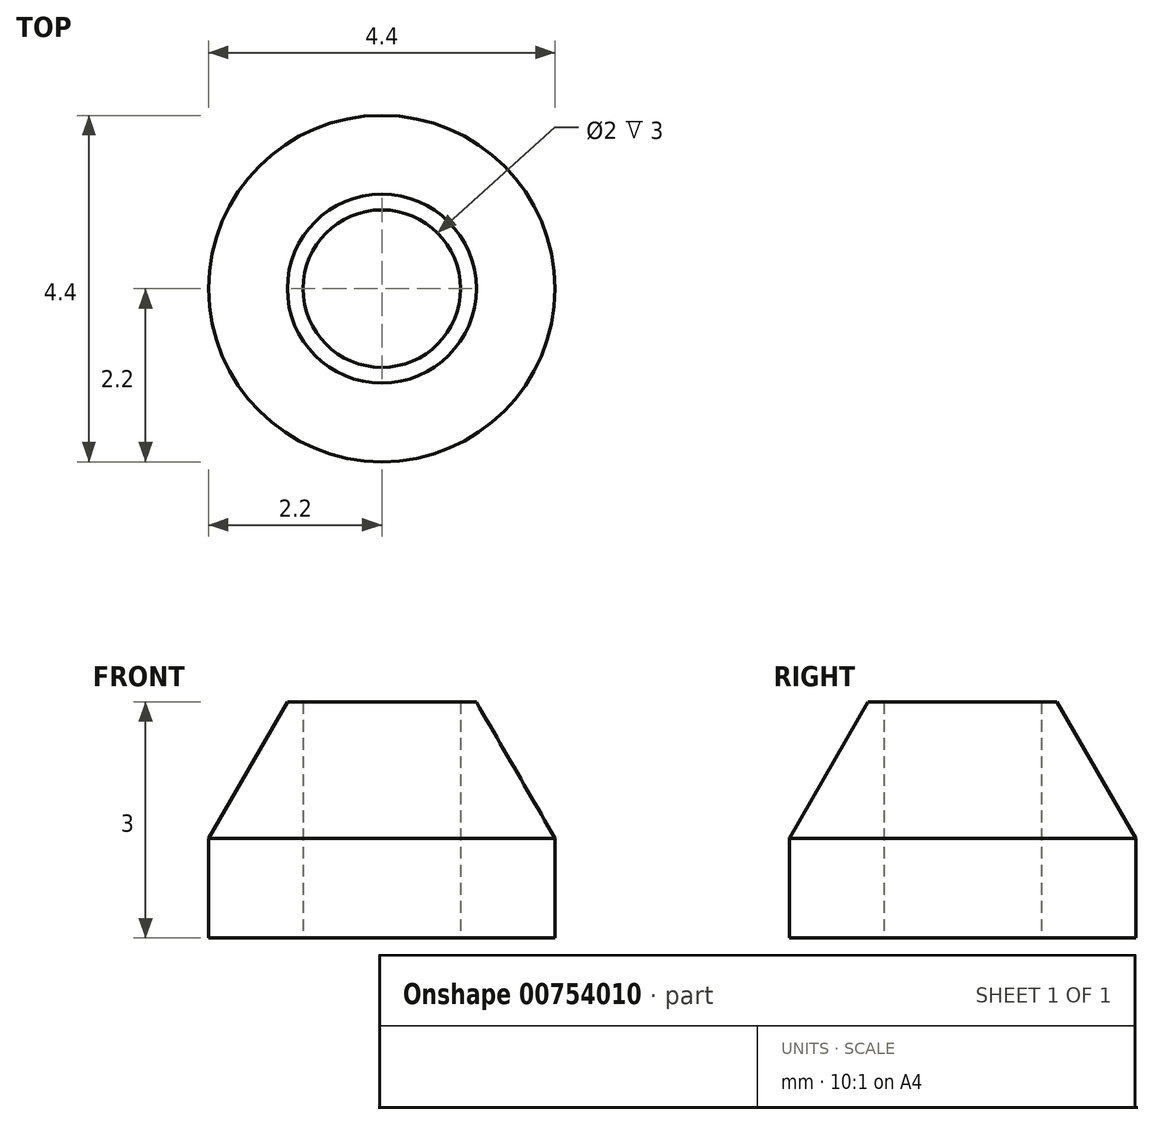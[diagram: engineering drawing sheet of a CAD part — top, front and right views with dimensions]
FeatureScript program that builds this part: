
annotation { "Feature Type Name" : "Feature", "Feature Type Description" : "" }
export const myFeature = defineFeature(function(context is Context, id is Id, definition is map)
    precondition{}
    {
        {
            var Q0;
            Q0=qCreatedBy(makeId("Top.planeOp"),FACE);
            var sketch = newSketch(context, id + "F0", { "sketchPlane" : qUnion([Q0])});
            skCircle(sketch, "E0", {"center": v(0, 0) * mm, "radius": 2.2 * mm});
            skCircle(sketch, "E1", {"center": v(0, 0) * mm, "radius": 1 * mm});
            skSolve(sketch);
        }
        {
            var Q0;
            Q0 = qSketchRegion(id + "F0", true);
            extrude(context, id + "F1", {"entities" : qUnion([Q0]), "depth" : 3 * mm, "offsetDistance" : 25 * mm});
        }
        {
            var Q0;
            Q0=makeQuery(id+"F1.opExtrude","CAP_EDGE",EDGE,{"disambiguationData":[OSD([sQuery(id+"F0.wireOp",EDGE,"E0")])],"isStart":false});
            chamfer(context, id + "F2", {"entities" : qUnion([Q0]), "chamferType" : ChamferType.OFFSET_ANGLE, "width" : 1 * mm, "oppositeDirection" : false, "angle" : 60 * degree, "tangentPropagation" : true});
        }
    });
